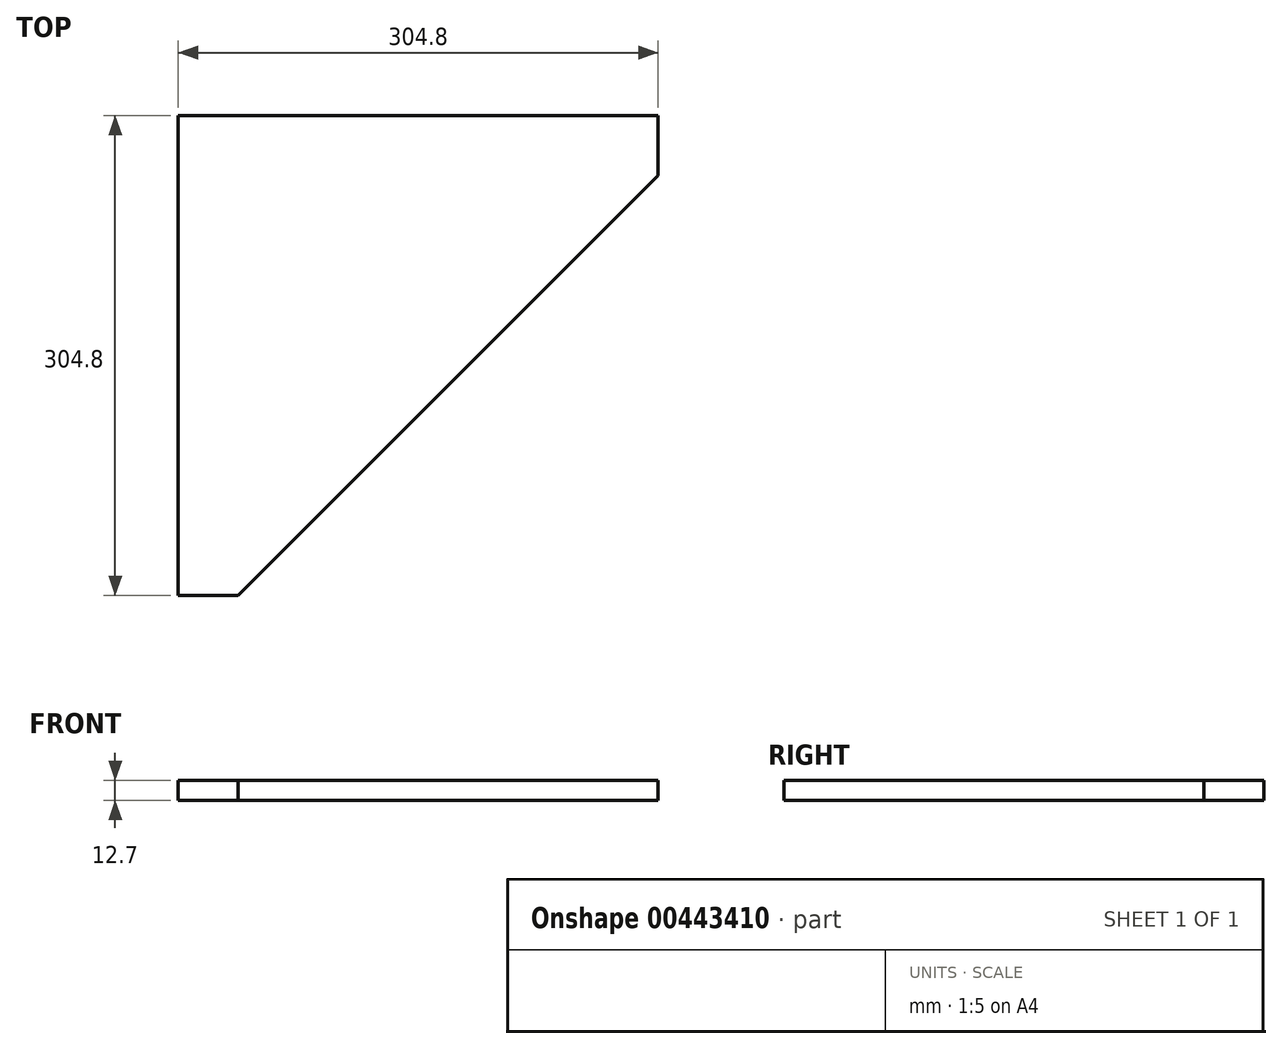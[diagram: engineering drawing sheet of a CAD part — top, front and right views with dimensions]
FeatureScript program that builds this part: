
annotation { "Feature Type Name" : "Feature", "Feature Type Description" : "" }
export const myFeature = defineFeature(function(context is Context, id is Id, definition is map)
    precondition{}
    {
        {
            var Q0;
            Q0=qCreatedBy(makeId("Top.planeOp"),FACE);
            var sketch = newSketch(context, id + "F0", { "sketchPlane" : qUnion([Q0])});
            skLineSegment(sketch, "E0", {"start": v(0, 0) * mm, "end": v(304.8, 0) * mm});
            skLineSegment(sketch, "E1", {"start": v(304.8, 0) * mm, "end": v(304.8, -38.1) * mm});
            skLineSegment(sketch, "E2", {"start": v(0, 0) * mm, "end": v(403.82, -403.82) * mm, "construction": true});
            skLineSegment(sketch, "E3.MirrorCS", {"start": v(0, 0) * mm, "end": v(0, -304.8) * mm});
            skLineSegment(sketch, "E4.MirrorCS", {"start": v(0, -304.8) * mm, "end": v(38.1, -304.8) * mm});
            skLineSegment(sketch, "E5", {"start": v(38.1, -304.8) * mm, "end": v(304.8, -38.1) * mm});
            skSolve(sketch);
        }
        {
            var Q0;
            Q0 = qSketchRegion(id + "F0", true);
            extrude(context, id + "F1", {"entities" : qUnion([Q0]), "depth" : 12.7 * mm});
        }
    });
